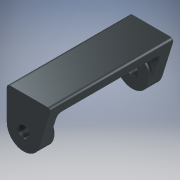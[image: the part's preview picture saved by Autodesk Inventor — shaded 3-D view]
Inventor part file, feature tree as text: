
AUTODESK INVENTOR PART (.ipt)
format: ipt  version: 2020 (Build 240168000, 168)  size: 217,600 bytes
history: native  units: in
note: dims shown in document units (in); Inventor stores cm internally (conversion verified against a paired STEP export)
features: sketch x4, extrude x3, fillet x2, hole x1, mirror x1
ambient origin geometry x8: Origin, YZ Plane, XZ Plane, XY Plane, X Axis, Y Axis, Z Axis, Center Point
bodies: Solid1 (feature_tree)
feature tree (11):
  extrude  "Extrusion1"  Depth=1.0in
  extrude  "Extrusion2"  Depth=0.0625in
  extrude  "Extrusion3"  Depth=0.25in
  hole  "Hole1"  [1 undecoded]
  mirror  "Mirror1"
  fillet  "Fillet1"  [1 undecoded]
  fillet  "Fillet2"  Radius=0.75in
  sketch  "Sketch1"  dims[d0=0.375in d1=1.0in]
  sketch  "Sketch2"  dims[d2=0.75in d3=0.0625in]
  sketch  "Sketch3"  dims[d4=2.75in d5=0.0in d6=0.25in]
  sketch  "Sketch4"  dims[d7=0.25in d8=0.25in d9=0.0in d10=0.0in d11=0.75in d12=0.3125in d13=0.0in d14=0.2656in d15=0.75in d16=0.375in d17=0.25in d18=0.5635in d19=1.0in d20=0.8108in d21=0.0625in d22=0.0625in]
note: 2 required parameter values undecoded (feature->parameter linkage not recoverable at this tier; creation-order binding heuristic only, values carry confidence <= 0.55)
